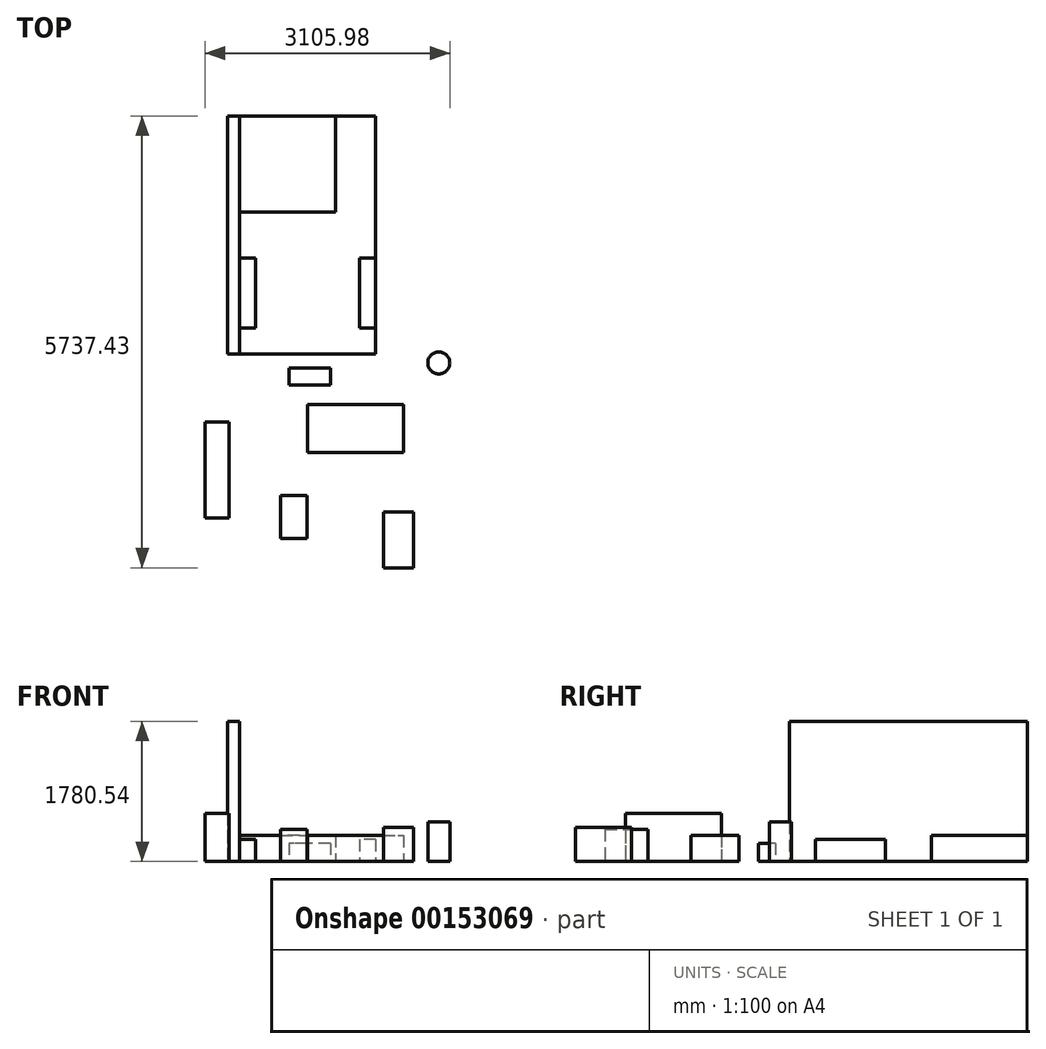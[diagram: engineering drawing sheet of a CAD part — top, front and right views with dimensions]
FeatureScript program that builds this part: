
annotation { "Feature Type Name" : "Feature", "Feature Type Description" : "" }
export const myFeature = defineFeature(function(context is Context, id is Id, definition is map)
    precondition{}
    {
        {
            var Q0;
            Q0=qCreatedBy(makeId("Top.planeOp"),FACE);
            var sketch = newSketch(context, id + "F0", { "sketchPlane" : qUnion([Q0])});
            skLineSegment(sketch, "E0.bottom", {"start": v(863.6, -1511.3) * mm, "end": v(-863.6, -1511.3) * mm});
            skLineSegment(sketch, "E0.top", {"start": v(863.6, 1511.3) * mm, "end": v(-863.6, 1511.3) * mm});
            skLineSegment(sketch, "E0.left", {"start": v(863.6, -1511.3) * mm, "end": v(863.6, 1511.3) * mm});
            skLineSegment(sketch, "E0.right", {"start": v(-863.6, -1511.3) * mm, "end": v(-863.6, 1511.3) * mm});
            skPoint(sketch, "E0.middle", {"position": v(0, 0) * mm});
            skLineSegment(sketch, "E1", {"start": v(-863.6, -1511.3) * mm, "end": v(-863.6, -1181.1) * mm});
            skLineSegment(sketch, "E2.bottom", {"start": v(-863.6, -1181.1) * mm, "end": v(-660.4, -1181.1) * mm});
            skLineSegment(sketch, "E2.top", {"start": v(-863.6, -292.1) * mm, "end": v(-660.4, -292.1) * mm});
            skLineSegment(sketch, "E2.left", {"start": v(-863.6, -1181.1) * mm, "end": v(-863.6, -292.1) * mm});
            skLineSegment(sketch, "E2.right", {"start": v(-660.4, -1181.1) * mm, "end": v(-660.4, -292.1) * mm});
            skLineSegment(sketch, "E3", {"start": v(-863.6, -292.1) * mm, "end": v(-863.6, 419.1) * mm});
            skLineSegment(sketch, "E4", {"start": v(-863.6, 419.1) * mm, "end": v(-863.6, 1511.3) * mm});
            skSolve(sketch);
        }
        {
            var Q0;
            Q0=makeQuery(id+"F0.imprint","IMPRINT",FACE,{"disambiguationData":[TD([[makeQuery(id+"F0.imprint","IMPRINT",EDGE,{"derivedFrom":sQuery(id+"F0.wireOp",EDGE,"E2.bottom")}),1.0]])]});
            extrude(context, id + "F1", {"entities" : qUnion([Q0]), "depth" : 279.4 * mm});
        }
        {
            var Q0;
            Q0=makeQuery(id+"F1.opExtrude","SWEPT_BODY",BODY,{"disambiguationData":[OSD([sQuery(id+"F0.wireOp",EDGE,"E2.bottom"),sQuery(id+"F0.wireOp",EDGE,"E2.top"),sQuery(id+"F0.wireOp",EDGE,"E2.left"),sQuery(id+"F0.wireOp",EDGE,"E2.right")])]});
            var Q1;
            Q1=qCreatedBy(makeId("Right.planeOp"),FACE);
            mirror(context, id + "F2", {"entities" : qUnion([Q0]), "mirrorPlane" : qUnion([Q1])});
        }
        {
            var Q0;
            Q0=makeQuery(id+"F0.imprint","IMPRINT",FACE,{"disambiguationData":[TD([[makeQuery(id+"F0.imprint","IMPRINT",EDGE,{"derivedFrom":sQuery(id+"F0.wireOp",EDGE,"E0.bottom")}),-1.0]])]});
            var sketch = newSketch(context, id + "F3", { "sketchPlane" : qUnion([Q0])});
            skSolve(sketch);
        }
        {
            var Q0;
            Q0=makeQuery(id+"F3.imprint","IMPRINT",FACE,{"disambiguationData":[TD([[makeQuery(id+"F3.imprint","IMPRINT",EDGE,{"derivedFrom":makeQuery(id+"F0.imprint","IMPRINT",EDGE,{"derivedFrom":sQuery(id+"F0.wireOp",EDGE,"E0.bottom")})}),-1.0]])]});
            extrude(context, id + "F4", {"entities" : qUnion([Q0]), "depth" : 2.54 * mm});
        }
        {
            var Q0;
            Q0=makeQuery(id+"F4.opExtrude","CAP_FACE",FACE,{"disambiguationData":[OSD([sQuery(id+"F0.wireOp",EDGE,"E0.bottom"),sQuery(id+"F0.wireOp",EDGE,"E0.top"),sQuery(id+"F0.wireOp",EDGE,"E0.left"),sQuery(id+"F0.wireOp",EDGE,"E1"),sQuery(id+"F0.wireOp",EDGE,"E2.bottom"),sQuery(id+"F0.wireOp",EDGE,"E2.top"),sQuery(id+"F0.wireOp",EDGE,"E2.right"),sQuery(id+"F0.wireOp",EDGE,"E3"),sQuery(id+"F0.wireOp",EDGE,"E4")])],"isStart":false});
            var sketch = newSketch(context, id + "F5", { "sketchPlane" : qUnion([Q0])});
            skLineSegment(sketch, "E5.bottom", {"start": v(-863.6, -1511.3) * mm, "end": v(-1016, -1511.3) * mm});
            skLineSegment(sketch, "E5.top", {"start": v(-863.6, 1511.3) * mm, "end": v(-1016, 1511.3) * mm});
            skLineSegment(sketch, "E5.left", {"start": v(-863.6, -1511.3) * mm, "end": v(-863.6, 1511.3) * mm});
            skLineSegment(sketch, "E5.right", {"start": v(-1016, -1511.3) * mm, "end": v(-1016, 1511.3) * mm});
            skSolve(sketch);
        }
        {
            var Q0;
            {var subQ4=sQuery(id+"F5.wireOp",EDGE,"E5.bottom");Q0=makeQuery(id+"F5.imprint","IMPRINT",FACE,{"disambiguationData":[TD([[makeQuery(id+"F5.imprint","IMPRINT",EDGE,{"derivedFrom":subQ4}),-1.0]])]});}
            extrude(context, id + "F6", {"entities" : qUnion([Q0]), "depth" : 1778 * mm});
        }
        {
            var Q0;
            Q0=makeQuery(id+"F4.opExtrude","CAP_FACE",FACE,{"disambiguationData":[OSD([sQuery(id+"F0.wireOp",EDGE,"E0.bottom"),sQuery(id+"F0.wireOp",EDGE,"E0.top"),sQuery(id+"F0.wireOp",EDGE,"E0.left"),sQuery(id+"F0.wireOp",EDGE,"E1"),sQuery(id+"F0.wireOp",EDGE,"E2.bottom"),sQuery(id+"F0.wireOp",EDGE,"E2.top"),sQuery(id+"F0.wireOp",EDGE,"E2.right"),sQuery(id+"F0.wireOp",EDGE,"E3"),sQuery(id+"F0.wireOp",EDGE,"E4")])],"isStart":false});
            var sketch = newSketch(context, id + "F7", { "sketchPlane" : qUnion([Q0])});
            skLineSegment(sketch, "E6.bottom", {"start": v(-863.6, 1511.3) * mm, "end": v(355.6, 1511.3) * mm});
            skLineSegment(sketch, "E6.top", {"start": v(-863.6, 292.1) * mm, "end": v(355.6, 292.1) * mm});
            skLineSegment(sketch, "E6.left", {"start": v(-863.6, 1511.3) * mm, "end": v(-863.6, 292.1) * mm});
            skLineSegment(sketch, "E6.right", {"start": v(355.6, 1511.3) * mm, "end": v(355.6, 292.1) * mm});
            skSolve(sketch);
        }
        {
            var Q0;
            Q0 = qSketchRegion(id + "F7", true);
            extrude(context, id + "F8", {"entities" : qUnion([Q0]), "depth" : 330.2 * mm});
        }
        {
            var Q0;
            Q0=makeQuery(id+"F0.imprint","IMPRINT",FACE,{"disambiguationData":[TD([[makeQuery(id+"F0.imprint","IMPRINT",EDGE,{"derivedFrom":sQuery(id+"F0.wireOp",EDGE,"E0.bottom")}),-1.0]])]});
            var sketch = newSketch(context, id + "F9", { "sketchPlane" : qUnion([Q0])});
            skLineSegment(sketch, "E7.bottom", {"start": v(-996.9, -3596.44) * mm, "end": v(-1301.7, -3596.44) * mm});
            skLineSegment(sketch, "E7.top", {"start": v(-996.9, -2377.24) * mm, "end": v(-1301.7, -2377.24) * mm});
            skLineSegment(sketch, "E7.left", {"start": v(-996.9, -3596.44) * mm, "end": v(-996.9, -2377.24) * mm});
            skLineSegment(sketch, "E7.right", {"start": v(-1301.7, -3596.44) * mm, "end": v(-1301.7, -2377.24) * mm});
            skSolve(sketch);
        }
        {
            var Q0;
            Q0 = qSketchRegion(id + "F9", true);
            extrude(context, id + "F10", {"entities" : qUnion([Q0]), "depth" : 609.6 * mm});
        }
        {
            var Q0;
            {var subQ4=sQuery(id+"F7.wireOp",EDGE,"E6.top");Q0=makeQuery(id+"F7.imprint","IMPRINT",FACE,{"disambiguationData":[TD([[makeQuery(id+"F7.imprint","IMPRINT",EDGE,{"derivedFrom":subQ4}),-1.0]])]});}
            var sketch = newSketch(context, id + "F11", { "sketchPlane" : qUnion([Q0])});
            skLineSegment(sketch, "E8.bottom", {"start": v(288.73, -1686.9) * mm, "end": v(-239.6, -1686.9) * mm});
            skLineSegment(sketch, "E8.top", {"start": v(288.73, -1907.88) * mm, "end": v(-239.6, -1907.88) * mm});
            skLineSegment(sketch, "E8.left", {"start": v(288.73, -1686.9) * mm, "end": v(288.73, -1907.88) * mm});
            skLineSegment(sketch, "E8.right", {"start": v(-239.6, -1686.9) * mm, "end": v(-239.6, -1907.88) * mm});
            skSolve(sketch);
        }
        {
            var Q0;
            Q0 = qSketchRegion(id + "F11", true);
            extrude(context, id + "F12", {"entities" : qUnion([Q0]), "depth" : 228.6 * mm});
        }
        {
            var Q0;
            Q0 = qSketchRegion(id + "F0", true);
            var sketch = newSketch(context, id + "F13", { "sketchPlane" : qUnion([Q0])});
            skLineSegment(sketch, "E9.bottom", {"start": v(0, -2151.76) * mm, "end": v(1219.2, -2151.76) * mm});
            skLineSegment(sketch, "E9.top", {"start": v(0, -2761.36) * mm, "end": v(1219.2, -2761.36) * mm});
            skLineSegment(sketch, "E9.left", {"start": v(0, -2151.76) * mm, "end": v(0, -2761.36) * mm});
            skLineSegment(sketch, "E9.right", {"start": v(1219.2, -2151.76) * mm, "end": v(1219.2, -2761.36) * mm});
            skSolve(sketch);
        }
        {
            var Q0;
            Q0=makeQuery(id+"F13.imprint","IMPRINT",FACE,{"disambiguationData":[TD([[makeQuery(id+"F13.imprint","IMPRINT",EDGE,{"derivedFrom":sQuery(id+"F13.wireOp",EDGE,"E9.bottom")}),-1.0]])]});
            extrude(context, id + "F14", {"entities" : qUnion([Q0]), "depth" : 330.2 * mm});
        }
        {
            var Q0;
            {var subQ1=makeQuery(id+"F4.opExtrude","CAP_EDGE",EDGE,{"disambiguationData":[OSD([sQuery(id+"F0.wireOp",EDGE,"E0.bottom")])],"isStart":false});Q0=makeQuery(id+"F5.imprint","IMPRINT",FACE,{"disambiguationData":[TD([[makeQuery(id+"F5.imprint","IMPRINT",EDGE,{"derivedFrom":subQ1}),-1.0]])]});}
            var sketch = newSketch(context, id + "F15", { "sketchPlane" : qUnion([Q0])});
            skLineSegment(sketch, "E10.bottom", {"start": v(-10.76, -3853.53) * mm, "end": v(-343.5, -3853.53) * mm});
            skLineSegment(sketch, "E10.top", {"start": v(-10.76, -3308.7) * mm, "end": v(-343.5, -3308.7) * mm});
            skLineSegment(sketch, "E10.left", {"start": v(-10.76, -3853.53) * mm, "end": v(-10.76, -3308.7) * mm});
            skLineSegment(sketch, "E10.right", {"start": v(-343.5, -3853.53) * mm, "end": v(-343.5, -3308.7) * mm});
            skSolve(sketch);
        }
        {
            var Q0;
            Q0 = qSketchRegion(id + "F15", true);
            extrude(context, id + "F16", {"entities" : qUnion([Q0]), "depth" : 403.86 * mm});
        }
        {
            var Q0;
            {var subQ1=makeQuery(id+"F4.opExtrude","CAP_EDGE",EDGE,{"disambiguationData":[OSD([sQuery(id+"F0.wireOp",EDGE,"E0.bottom")])],"isStart":false});Q0=makeQuery(id+"F5.imprint","IMPRINT",FACE,{"disambiguationData":[TD([[makeQuery(id+"F5.imprint","IMPRINT",EDGE,{"derivedFrom":subQ1}),-1.0]])]});}
            var sketch = newSketch(context, id + "F17", { "sketchPlane" : qUnion([Q0])});
            skLineSegment(sketch, "E11.bottom", {"start": v(1342.8, -4226.13) * mm, "end": v(961.8, -4226.13) * mm});
            skLineSegment(sketch, "E11.top", {"start": v(1342.8, -3520) * mm, "end": v(961.8, -3520) * mm});
            skLineSegment(sketch, "E11.left", {"start": v(1342.8, -4226.13) * mm, "end": v(1342.8, -3520) * mm});
            skLineSegment(sketch, "E11.right", {"start": v(961.8, -4226.13) * mm, "end": v(961.8, -3520) * mm});
            skSolve(sketch);
        }
        {
            var Q0;
            Q0 = qSketchRegion(id + "F17", true);
            extrude(context, id + "F18", {"entities" : qUnion([Q0]), "depth" : 429.26 * mm});
        }
        {
            var Q0;
            {var subQ1=makeQuery(id+"F4.opExtrude","CAP_EDGE",EDGE,{"disambiguationData":[OSD([sQuery(id+"F0.wireOp",EDGE,"E0.bottom")])],"isStart":false});Q0=makeQuery(id+"F5.imprint","IMPRINT",FACE,{"disambiguationData":[TD([[makeQuery(id+"F5.imprint","IMPRINT",EDGE,{"derivedFrom":subQ1}),-1.0]])]});}
            var sketch = newSketch(context, id + "F19", { "sketchPlane" : qUnion([Q0])});
            skCircle(sketch, "E12", {"center": v(1664.58, -1624.4) * mm, "radius": 139.7 * mm});
            skSolve(sketch);
        }
        {
            var Q0;
            Q0 = qSketchRegion(id + "F19", true);
            extrude(context, id + "F20", {"entities" : qUnion([Q0]), "depth" : 499.62 * mm});
        }
    });
